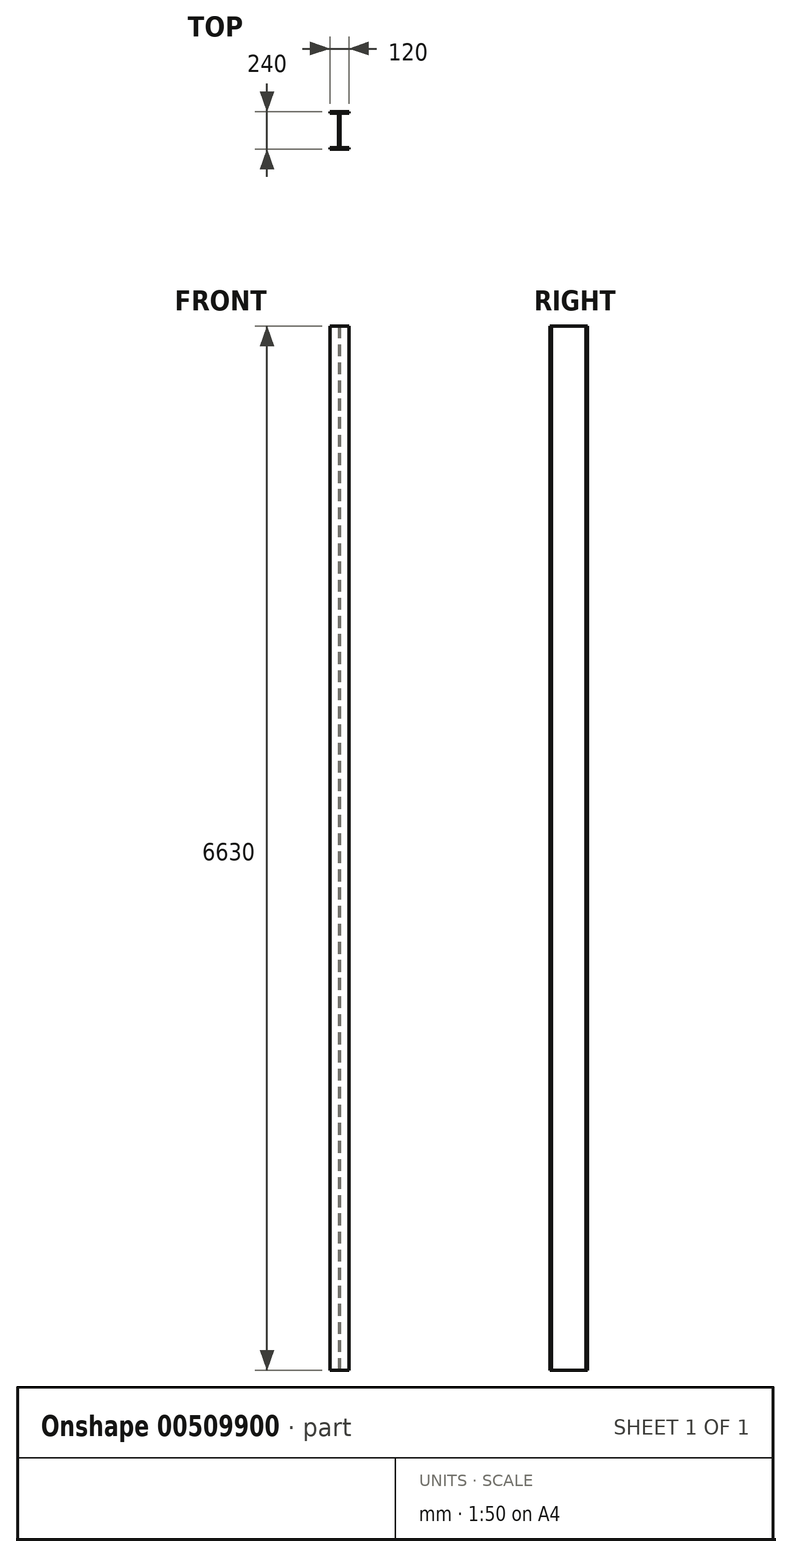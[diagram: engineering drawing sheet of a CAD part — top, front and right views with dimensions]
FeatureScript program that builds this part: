
annotation { "Feature Type Name" : "Feature", "Feature Type Description" : "" }
export const myFeature = defineFeature(function(context is Context, id is Id, definition is map)
    precondition{}
    {
        {
            var Q0;
            Q0=qCreatedBy(makeId("Top.planeOp"),FACE);
            var sketch = newSketch(context, id + "F0", { "sketchPlane" : qUnion([Q0])});
            skLineSegment(sketch, "E0", {"start": v(-26.31, -23.12) * mm, "end": v(93.69, -23.12) * mm});
            skLineSegment(sketch, "E1", {"start": v(-26.31, -23.12) * mm, "end": v(-26.31, -13.12) * mm});
            skLineSegment(sketch, "E2", {"start": v(-26.31, -13.12) * mm, "end": v(28.69, -13.12) * mm});
            skLineSegment(sketch, "E3", {"start": v(28.69, -13.12) * mm, "end": v(28.69, 206.88) * mm});
            skLineSegment(sketch, "E4", {"start": v(28.69, 206.88) * mm, "end": v(-26.31, 206.88) * mm});
            skLineSegment(sketch, "E5", {"start": v(-26.31, 206.88) * mm, "end": v(-26.31, 216.88) * mm});
            skLineSegment(sketch, "E6", {"start": v(-26.31, 216.88) * mm, "end": v(93.69, 216.88) * mm});
            skLineSegment(sketch, "E7", {"start": v(93.69, 216.88) * mm, "end": v(93.69, 206.88) * mm});
            skLineSegment(sketch, "E8", {"start": v(93.69, 206.88) * mm, "end": v(38.69, 206.88) * mm});
            skLineSegment(sketch, "E9", {"start": v(38.69, 206.88) * mm, "end": v(38.69, -13.12) * mm});
            skLineSegment(sketch, "E10", {"start": v(38.69, -13.12) * mm, "end": v(93.69, -13.12) * mm});
            skLineSegment(sketch, "E11", {"start": v(93.69, -13.12) * mm, "end": v(93.69, -23.12) * mm});
            skSolve(sketch);
        }
        {
            var Q0;
            Q0=makeQuery(id+"F0.imprint","IMPRINT",FACE,{"disambiguationData":[TD([[makeQuery(id+"F0.imprint","IMPRINT",EDGE,{"derivedFrom":sQuery(id+"F0.wireOp",EDGE,"E0")}),1.0]])]});
            extrude(context, id + "F1", {"entities" : qUnion([Q0]), "depth" : 6630 * mm});
        }
    });
